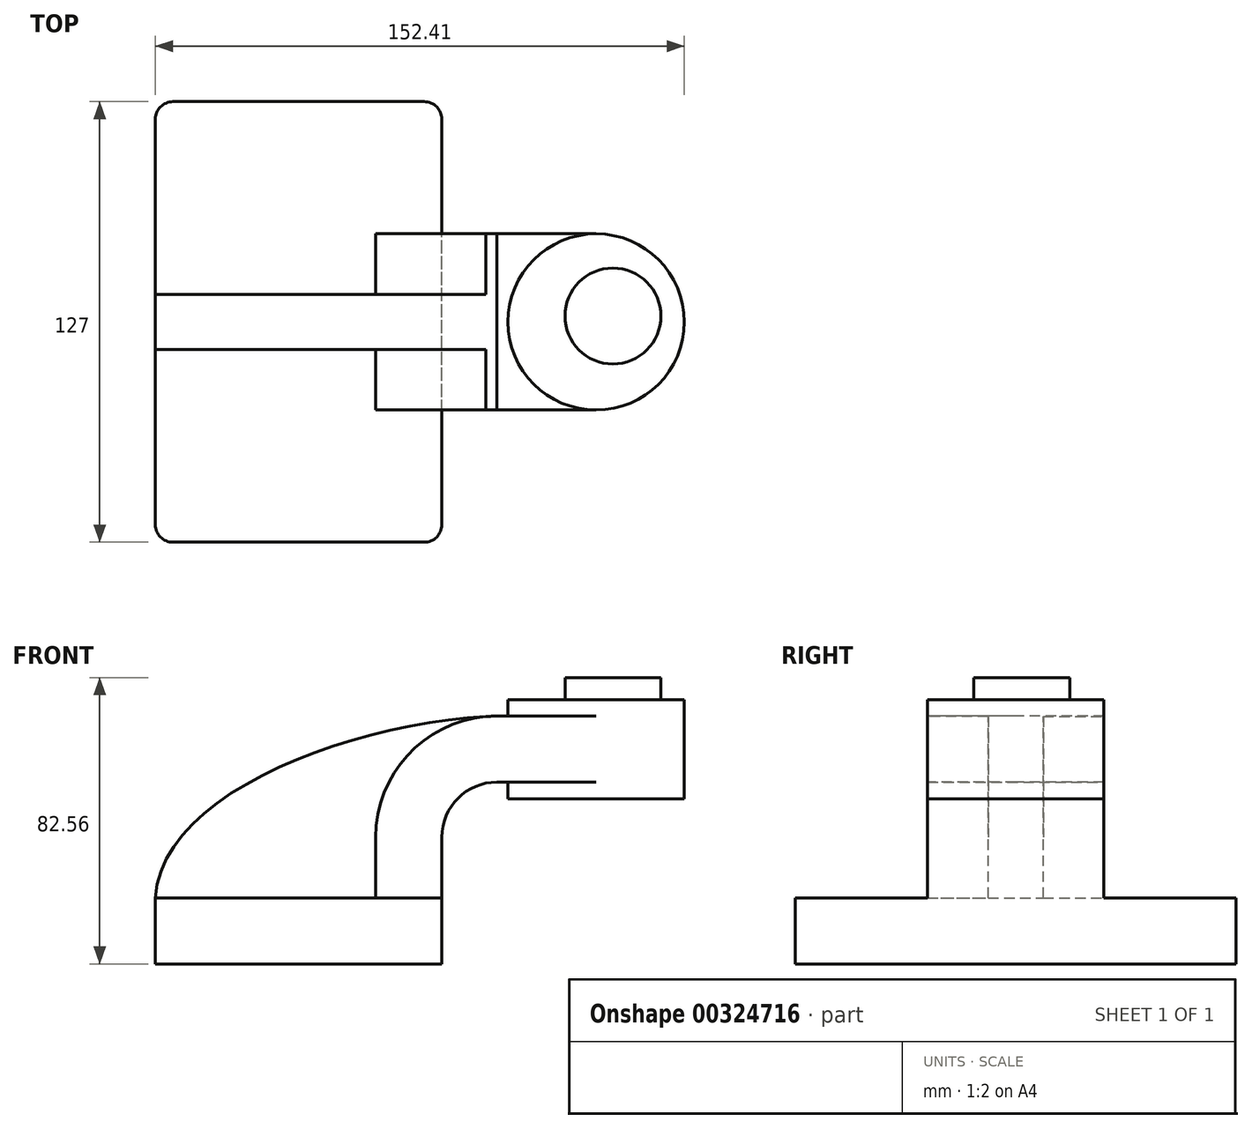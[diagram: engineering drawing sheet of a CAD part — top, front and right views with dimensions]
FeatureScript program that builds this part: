
annotation { "Feature Type Name" : "Feature", "Feature Type Description" : "" }
export const myFeature = defineFeature(function(context is Context, id is Id, definition is map)
    precondition{}
    {
        {
            var Q0;
            Q0=qCreatedBy(makeId("Front.planeOp"),FACE);
            var sketch = newSketch(context, id + "F0", { "sketchPlane" : qUnion([Q0])});
            skLineSegment(sketch, "E0.rect.bottom", {"start": v(-41.28, 9.52) * mm, "end": v(41.28, 9.52) * mm});
            skLineSegment(sketch, "E0.rect.top", {"start": v(-41.28, -9.52) * mm, "end": v(41.28, -9.52) * mm});
            skLineSegment(sketch, "E0.rect.left", {"start": v(-41.28, 9.52) * mm, "end": v(-41.28, -9.52) * mm});
            skLineSegment(sketch, "E0.rect.right", {"start": v(41.28, 9.52) * mm, "end": v(41.28, -9.52) * mm});
            skPoint(sketch, "E0.rect.middle", {"position": v(0, 0) * mm});
            skLineSegment(sketch, "E1", {"start": v(41.28, 9.52) * mm, "end": v(41.28, 27) * mm});
            skArc(sketch, "E2", {"start": v(41.28, 27) * mm, "mid": v(45.92, 38.23) * mm, "end": v(57.15, 42.88) * mm});
            skLineSegment(sketch, "E3", {"start": v(57.15, 42.88) * mm, "end": v(85.72, 42.88) * mm});
            skLineSegment(sketch, "E4.rect.bottom", {"start": v(60.32, 38.1) * mm, "end": v(111.12, 38.1) * mm});
            skLineSegment(sketch, "E4.rect.top", {"start": v(60.32, 66.68) * mm, "end": v(111.12, 66.68) * mm});
            skLineSegment(sketch, "E4.rect.left", {"start": v(60.32, 38.1) * mm, "end": v(60.32, 66.68) * mm});
            skLineSegment(sketch, "E4.rect.right", {"start": v(111.13, 38.1) * mm, "end": v(111.12, 66.68) * mm});
            skPoint(sketch, "E4.rect.middle", {"position": v(85.72, 52.39) * mm});
            skLineSegment(sketch, "E5.0", {"start": v(57.15, 61.93) * mm, "end": v(85.72, 61.93) * mm});
            skArc(sketch, "E5.1", {"start": v(22.23, 27) * mm, "mid": v(32.45, 51.7) * mm, "end": v(57.15, 61.93) * mm});
            skLineSegment(sketch, "E5.2", {"start": v(22.23, 9.52) * mm, "end": v(22.23, 27) * mm});
            skLineSegment(sketch, "E6", {"start": v(85.72, 38.1) * mm, "end": v(85.72, 66.68) * mm});
            skFitSpline(sketch, "E7", {"points": [v(-41.28, 9.53) * mm, v(57.15, 61.93) * mm], "startDerivative": vector(5.2, 92.34) * mm, "endDerivative": vector(120.92, 4.22) * mm});
            skSolve(sketch);
        }
        {
            var Q0;
            Q0=makeQuery(id+"F0.imprint","IMPRINT",FACE,{"disambiguationData":[TD([[makeQuery(id+"F0.imprint","IMPRINT",EDGE,{"derivedFrom":sQuery(id+"F0.wireOp",EDGE,"E0.rect.top")}),1.0]])]});
            extrude(context, id + "F1", {"entities" : qUnion([Q0]), "endBound" : BoundingType.SYMMETRIC, "depth" : 127 * mm});
        }
        {
            var Q0;
            {var subQ9=sQuery(id+"F0.wireOp",EDGE,"E1");Q0=makeQuery(id+"F0.imprint","IMPRINT",FACE,{"disambiguationData":[TD([[makeQuery(id+"F0.imprint","IMPRINT",EDGE,{"derivedFrom":subQ9}),1.0]])]});}
            var Q1;
            {var subQ0=sQuery(id+"F0.wireOp",EDGE,"E6");var subQ1=sQuery(id+"F0.wireOp",EDGE,"E3");var subQ2=makeQuery(id+"F0.imprint","INTERSECT",VERTEX,{"derivedFrom":[subQ1,subQ0]});Q1=makeQuery(id+"F0.imprint","IMPRINT",FACE,{"disambiguationData":[TD([[makeQuery(id+"F0.imprint","IMPRINT",EDGE,{"disambiguationData":[TD([[subQ2,1.0]])],"derivedFrom":subQ1}),1.0]])]});}
            extrude(context, id + "F2", {"entities" : qUnion([Q0, Q1]), "operationType" : NewBodyOperationType.ADD, "endBound" : BoundingType.SYMMETRIC, "depth" : 50.8 * mm});
        }
        {
            var Q0;
            {var subQ3=sQuery(id+"F0.wireOp",EDGE,"E5.2");Q0=makeQuery(id+"F0.imprint","IMPRINT",FACE,{"disambiguationData":[TD([[makeQuery(id+"F0.imprint","IMPRINT",EDGE,{"derivedFrom":subQ3}),1.0]])]});}
            extrude(context, id + "F3", {"entities" : qUnion([Q0]), "operationType" : NewBodyOperationType.ADD, "endBound" : BoundingType.SYMMETRIC, "depth" : 15.88 * mm});
        }
        {
            var Q0;
            {var subQ5=sQuery(id+"F0.wireOp",EDGE,"E4.rect.right");Q0=makeQuery(id+"F0.imprint","IMPRINT",FACE,{"disambiguationData":[TD([[makeQuery(id+"F0.imprint","IMPRINT",EDGE,{"derivedFrom":subQ5}),1.0]])]});}
            var Q1;
            Q1=sQuery(id+"F0.wireOp",EDGE,"E6");
            revolve(context, id + "F4", {"operationType" : NewBodyOperationType.ADD, "entities" : qUnion([Q0]), "axis" : qUnion([Q1]), "revolveType" : RevolveType.FULL});
        }
        {
            var Q0;
            Q0=makeQuery(id+"F1.opExtrude","CAP_EDGE",EDGE,{"disambiguationData":[OSD([sQuery(id+"F0.wireOp",EDGE,"E0.rect.right")])],"isStart":false});
            var Q1;
            Q1=makeQuery(id+"F1.opExtrude","CAP_EDGE",EDGE,{"disambiguationData":[OSD([sQuery(id+"F0.wireOp",EDGE,"E0.rect.left")])],"isStart":false});
            var Q2;
            Q2=makeQuery(id+"F1.opExtrude","CAP_EDGE",EDGE,{"disambiguationData":[OSD([sQuery(id+"F0.wireOp",EDGE,"E0.rect.right")])],"isStart":true});
            var Q3;
            Q3=makeQuery(id+"F1.opExtrude","CAP_EDGE",EDGE,{"disambiguationData":[OSD([sQuery(id+"F0.wireOp",EDGE,"E0.rect.left")])],"isStart":true});
            fillet(context, id + "F5", {"entities" : qUnion([Q0, Q1, Q2, Q3]), "radius" : 5.08 * mm, "tangentPropagation" : true, "allowEdgeOverflow" : false});
        }
        {
            var Q0;
            Q0=makeQuery(id+"F4.opRevolve","SWEPT_FACE",FACE,{"disambiguationData":[OSD([sQuery(id+"F0.wireOp",EDGE,"E4.rect.top")])]});
            var sketch = newSketch(context, id + "F6", { "sketchPlane" : qUnion([Q0])});
            skCircle(sketch, "E8", {"center": v(90.56, 1.71) * mm, "radius": 13.82 * mm});
            skSolve(sketch);
        }
        {
            var Q0;
            Q0=makeQuery(id+"F6.imprint","IMPRINT",FACE,{"disambiguationData":[TD([[makeQuery(id+"F6.imprint","IMPRINT",EDGE,{"derivedFrom":sQuery(id+"F6.wireOp",EDGE,"E8")}),1.0]])]});
            extrude(context, id + "F7", {"entities" : qUnion([Q0]), "operationType" : NewBodyOperationType.ADD, "depth" : 6.35 * mm});
        }
    });
